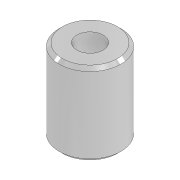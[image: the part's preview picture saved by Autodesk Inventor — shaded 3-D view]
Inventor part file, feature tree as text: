
AUTODESK INVENTOR PART (.ipt)
format: ipt  version: 2020 (Build 240168000, 168)  size: 106,496 bytes
history: native  units: mm
features: chamfer x1
ambient origin geometry x8: Origin, YZ Plane, XZ Plane, XY Plane, X Axis, Y Axis, Z Axis, Center Point
bodies: Solid1 (feature_tree)
feature tree (1):
  chamfer  "Chamfer1"  [1 undecoded]
note: 1 required parameter value undecoded (feature->parameter linkage not recoverable at this tier; creation-order binding heuristic only, values carry confidence <= 0.55)
